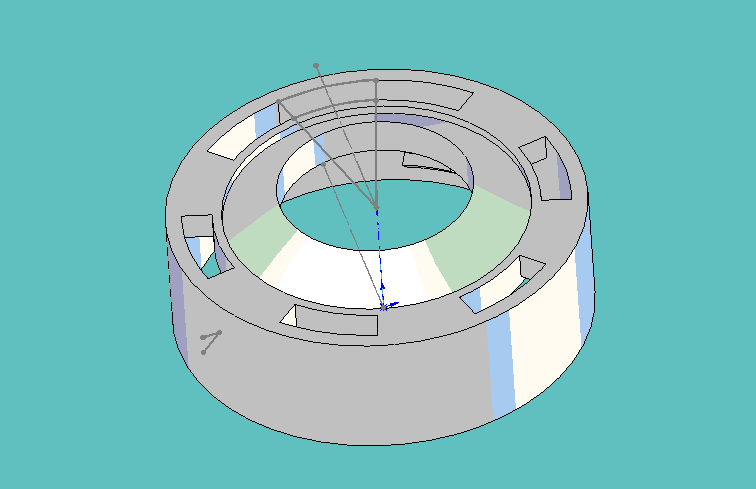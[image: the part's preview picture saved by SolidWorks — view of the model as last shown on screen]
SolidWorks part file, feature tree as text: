
SOLIDWORKS PART (.sldprt)
format: sldprt  version: not decoded by parser v0  size: 331,776 bytes
history: native  units: mm
features: sketch x10, plane x6, extrude x3, pattern_circular x2, material x1, revolve x1, cut_extrude x1 (+10 scaffold rows collapsed)
feature tree (34):
  scaffold x10  (default folders/planes/origin — collapsed)
  material  "Material <not specified>"
  plane  "Frontal"
  plane  "Horizontal"
  plane  "Profile"
  sketch  "Sketch1"  dims[D1=~32.193657mm]
  extrude  "Extrude1"  Depth=14mm
  sketch  "Sketch3"  dims[D1=2.0mm D2=2.0mm D3=1.8mm]
  sketch  "Sketch4"
  revolve  "Revolve6"  Angle=16deg
  pattern_circular  "CirPattern1"  Count=6 Angle=360deg
  plane  "Plane1"  Offset=10mm
  sketch  "Sketch5"  dims[D1=~18.027315mm]
  extrude  "Extrude2"  Depth=4mm
  plane  "Plane2"  Offset=1mm
  sketch  "Sketch6"
  plane  "Plane3"  Offset=3mm
  sketch  "Sketch7"  dims[D1=~10.307266mm]
  sketch  "Sketch8"
  cut_extrude  "Cut-Extrude1"  [1 undecoded]
  sketch  "Sketch9"  dims[c1.D1=2.0mm c2.D1=22.0deg c2.D2=~24.463253mm c3.D2=15.0deg c3.D3=~24.225178mm c4.D3=~162.810569deg c5.D3=~24.225178mm c6.D3=~166.629378deg c6.D4=20.75mm c7.D4=~13.370622deg c7.D3=~7.561286mm c8.D3=15.0deg]
  extrude  "Extrude3"  Depth=3mm
  sketch  "Sketch10"
  sketch  "Sketch12"
  pattern_circular  "CirPattern2"  Count=6 Angle=360deg
decode coverage: 11 of 17 modeling features carry decoded parameters
note: ~ marks probable driven/reference dimensions
note: 1 parameter value undecoded
note: suppression state not decoded; provenance and decode notes live in map.json
